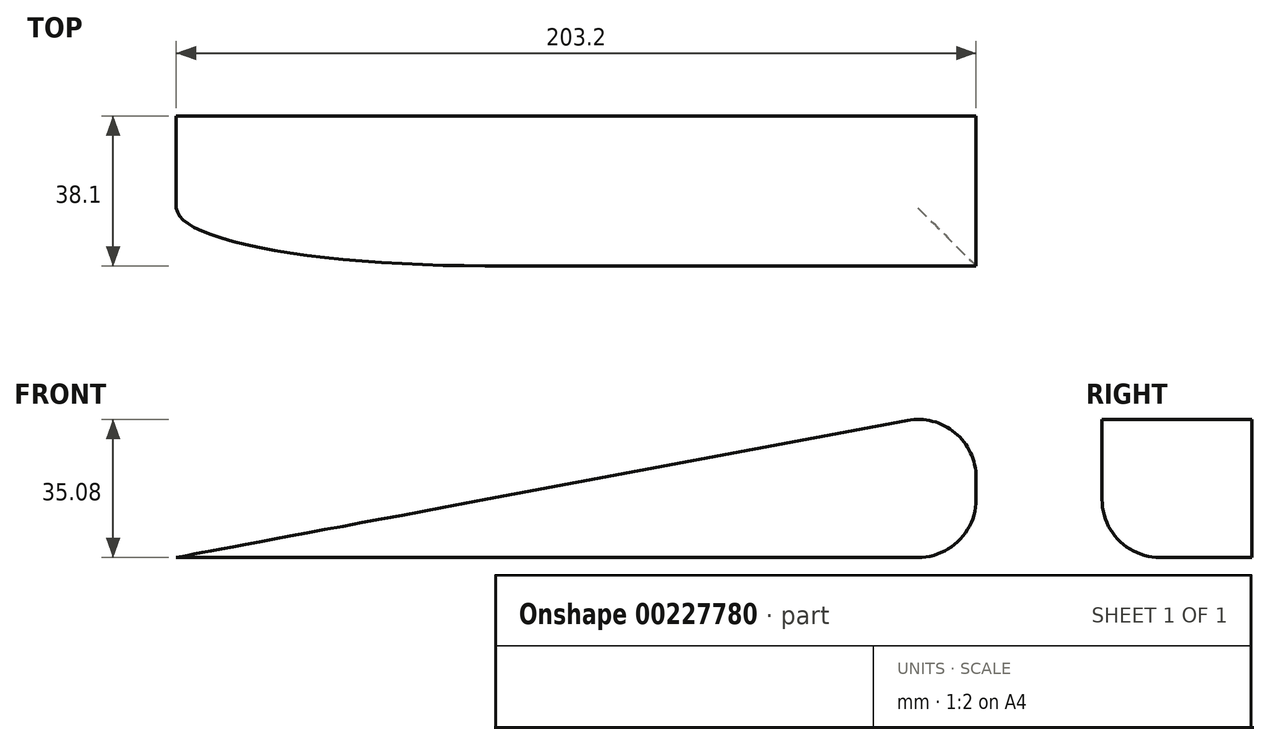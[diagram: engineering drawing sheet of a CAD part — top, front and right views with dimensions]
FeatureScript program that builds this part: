
annotation { "Feature Type Name" : "Feature", "Feature Type Description" : "" }
export const myFeature = defineFeature(function(context is Context, id is Id, definition is map)
    precondition{}
    {
        {
            var Q0;
            Q0=qCreatedBy(makeId("Front.planeOp"),FACE);
            var sketch = newSketch(context, id + "F0", { "sketchPlane" : qUnion([Q0])});
            skLineSegment(sketch, "E0", {"start": v(0, 0) * mm, "end": v(-101, 0) * mm});
            skLineSegment(sketch, "E1", {"start": v(-101, 0) * mm, "end": v(102.2, 0) * mm});
            skLineSegment(sketch, "E2", {"start": v(102.2, 0) * mm, "end": v(102.2, 38.1) * mm});
            skLineSegment(sketch, "E3", {"start": v(102.2, 38.1) * mm, "end": v(-101, 0) * mm});
            skSolve(sketch);
        }
        {
            var Q0;
            {var subQ2=sQuery(id+"F0.wireOp",EDGE,"E2");Q0=makeQuery(id+"F0.imprint","IMPRINT",FACE,{"disambiguationData":[TD([[makeQuery(id+"F0.imprint","IMPRINT",EDGE,{"derivedFrom":subQ2}),1.0]])]});}
            extrude(context, id + "F1", {"entities" : qUnion([Q0]), "depth" : 38.1 * mm});
        }
        {
            var Q0;
            Q0=makeQuery(id+"F1.opExtrude","SWEPT_EDGE",EDGE,{"disambiguationData":[OSD([sQuery(id+"F0.wireOp",EDGE,"E2"),sQuery(id+"F0.wireOp",EDGE,"E3")])]});
            var Q1;
            Q1=makeQuery(id+"F1.opExtrude","SWEPT_EDGE",EDGE,{"disambiguationData":[OSD([sQuery(id+"F0.wireOp",EDGE,"E1"),sQuery(id+"F0.wireOp",EDGE,"E2")])]});
            var Q2;
            Q2=makeQuery(id+"F1.opExtrude","CAP_EDGE",EDGE,{"disambiguationData":[OSD([sQuery(id+"F0.wireOp",EDGE,"E1")])],"isStart":false});
            fillet(context, id + "F2", {"entities" : qUnion([Q0, Q1, Q2]), "radius" : 14.72 * mm, "tangentPropagation" : true, "allowEdgeOverflow" : false});
        }
    });
